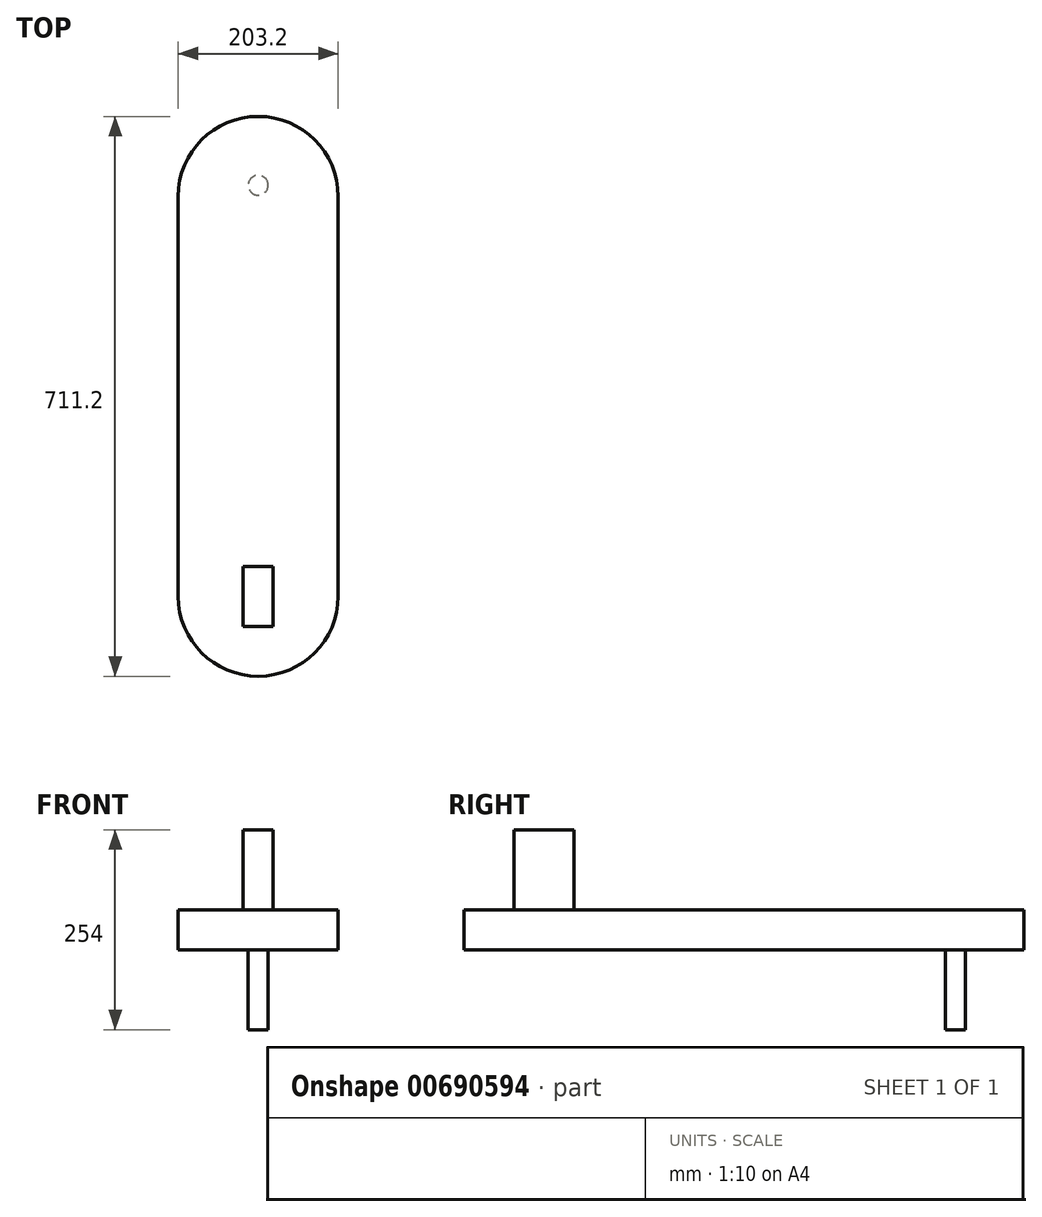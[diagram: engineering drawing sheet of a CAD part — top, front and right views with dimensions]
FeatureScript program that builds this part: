
annotation { "Feature Type Name" : "Feature", "Feature Type Description" : "" }
export const myFeature = defineFeature(function(context is Context, id is Id, definition is map)
    precondition{}
    {
        {
            var Q0;
            Q0=qCreatedBy(makeId("Top.planeOp"),FACE);
            var sketch = newSketch(context, id + "F0", { "sketchPlane" : qUnion([Q0])});
            skArc(sketch, "E0", {"start": v(-101.6, 0) * mm, "mid": v(0, -101.6) * mm, "end": v(101.6, 0) * mm});
            skLineSegment(sketch, "E1", {"start": v(101.6, 0) * mm, "end": v(101.6, 508) * mm});
            skArc(sketch, "E2", {"start": v(101.6, 508) * mm, "mid": v(0, 609.6) * mm, "end": v(-101.6, 508) * mm});
            skLineSegment(sketch, "E3", {"start": v(-101.6, 508) * mm, "end": v(-101.6, 0) * mm});
            skSolve(sketch);
        }
        {
            var Q0;
            Q0 = qSketchRegion(id + "F0", true);
            extrude(context, id + "F1", {"entities" : qUnion([Q0]), "oppositeDirection" : true, "depth" : 50.8 * mm, "offsetDistance" : 25.4 * mm});
        }
        {
            var Q0;
            Q0=makeQuery(id+"F1.opExtrude","CAP_FACE",FACE,{"disambiguationData":[OSD([sQuery(id+"F0.wireOp",EDGE,"E0"),sQuery(id+"F0.wireOp",EDGE,"E1"),sQuery(id+"F0.wireOp",EDGE,"E2"),sQuery(id+"F0.wireOp",EDGE,"E3")])],"isStart":false});
            var sketch = newSketch(context, id + "F2", { "sketchPlane" : qUnion([Q0])});
            skCircle(sketch, "E4", {"center": v(0, -522.22) * mm, "radius": 12.7 * mm});
            skPoint(sketch, "E4.centerSnap0", {"position": v(0, -609.6) * mm});
            skSolve(sketch);
        }
        {
            var Q0;
            Q0 = qSketchRegion(id + "F2", true);
            extrude(context, id + "F3", {"entities" : qUnion([Q0]), "operationType" : NewBodyOperationType.ADD, "depth" : 101.6 * mm, "offsetDistance" : 25.4 * mm});
        }
        {
            var Q0;
            Q0=makeQuery(id+"F1.opExtrude","CAP_FACE",FACE,{"disambiguationData":[OSD([sQuery(id+"F0.wireOp",EDGE,"E0"),sQuery(id+"F0.wireOp",EDGE,"E1"),sQuery(id+"F0.wireOp",EDGE,"E2"),sQuery(id+"F0.wireOp",EDGE,"E3")])],"isStart":true});
            var sketch = newSketch(context, id + "F4", { "sketchPlane" : qUnion([Q0])});
            skLineSegment(sketch, "E5.bottom", {"start": v(-19.05, -38.1) * mm, "end": v(19.05, -38.1) * mm});
            skLineSegment(sketch, "E5.top", {"start": v(-19.05, 38.1) * mm, "end": v(19.05, 38.1) * mm});
            skLineSegment(sketch, "E5.left", {"start": v(-19.05, -38.1) * mm, "end": v(-19.05, 38.1) * mm});
            skLineSegment(sketch, "E5.right", {"start": v(19.05, -38.1) * mm, "end": v(19.05, 38.1) * mm});
            skSolve(sketch);
        }
        {
            var Q0;
            Q0 = qSketchRegion(id + "F4", true);
            extrude(context, id + "F5", {"entities" : qUnion([Q0]), "operationType" : NewBodyOperationType.ADD, "depth" : 101.6 * mm, "offsetDistance" : 25.4 * mm});
        }
    });
